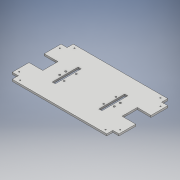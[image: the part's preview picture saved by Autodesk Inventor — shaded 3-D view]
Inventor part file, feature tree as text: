
AUTODESK INVENTOR PART (.ipt)
format: ipt  version: 2017 (Build 210142000, 142)  size: 224,256 bytes
history: native  units: mm
features: sketch x5, extrude x3, hole x2
ambient origin geometry x8: Origin, YZ Plane, XZ Plane, XY Plane, X Axis, Y Axis, Z Axis, Center Point
bodies: Body1 (feature_tree)
feature tree (10):
  extrude  "Extrusion2"  Depth=350.0mm
  extrude  "Extrusion3"  Depth=200.0mm
  hole  "Perçage2"  [1 undecoded]
  extrude  "Extrusion4"  Depth=20.0mm
  hole  "Perçage3"  [1 undecoded]
  sketch  "Esquisse1"
  sketch  "Esquisse3"
  sketch  "Esquisse4"
  sketch  "Esquisse5"
  sketch  "Esquisse6"
note: 2 required parameter values undecoded (feature->parameter linkage not recoverable at this tier; creation-order binding heuristic only, values carry confidence <= 0.55)
